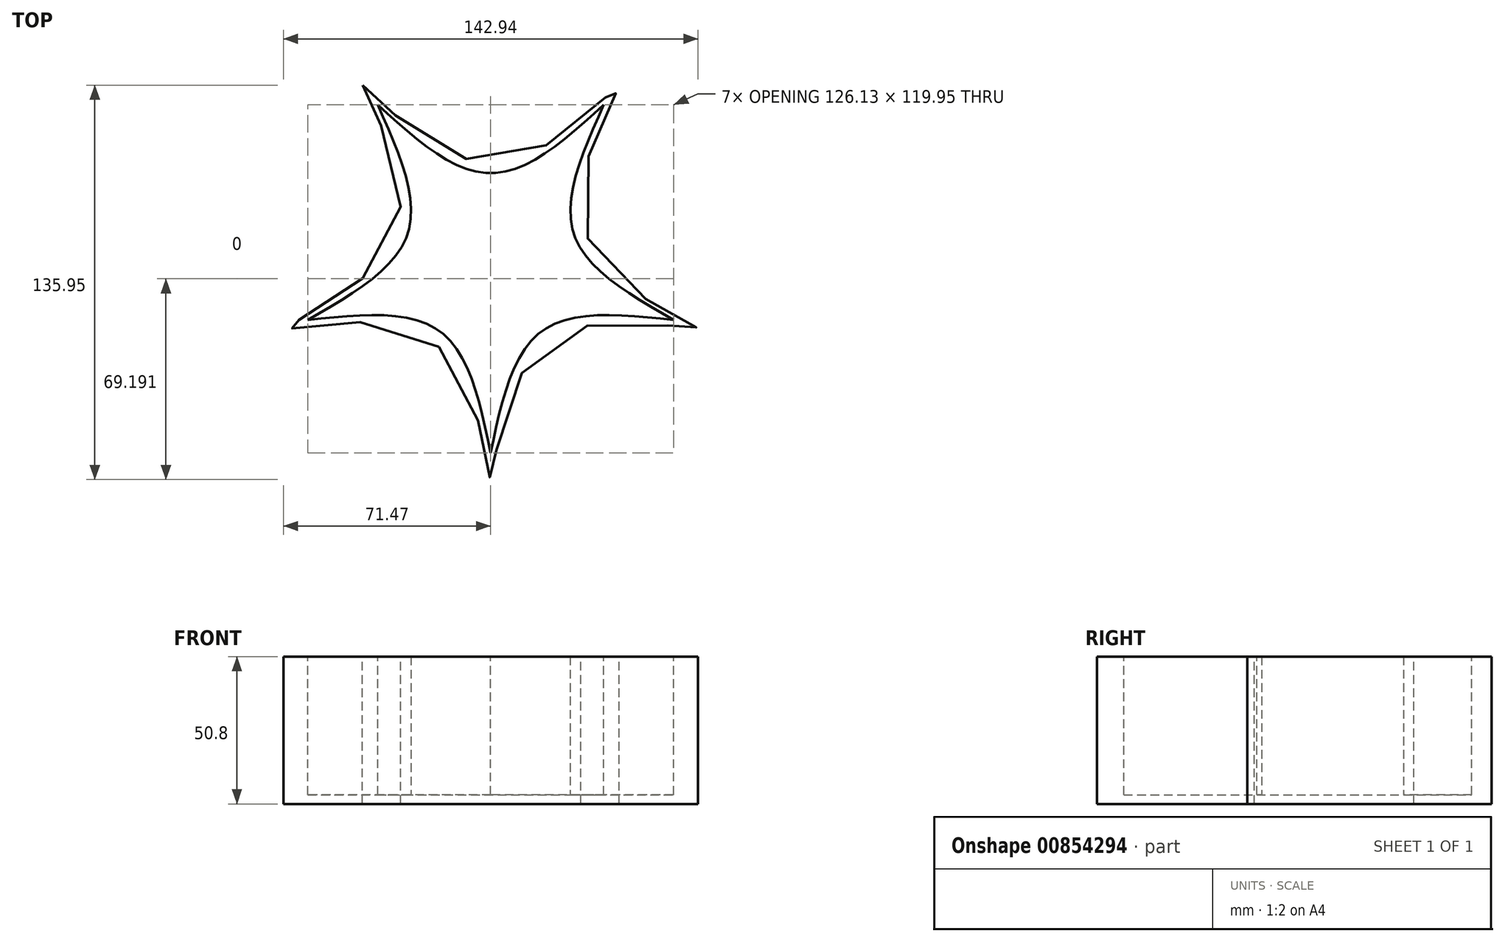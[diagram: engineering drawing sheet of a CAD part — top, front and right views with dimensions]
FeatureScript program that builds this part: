
annotation { "Feature Type Name" : "Feature", "Feature Type Description" : "" }
export const myFeature = defineFeature(function(context is Context, id is Id, definition is map)
    precondition{}
    {
        {
            var Q0;
            Q0=qCreatedBy(makeId("Top.planeOp"),FACE);
            var sketch = newSketch(context, id + "F0", { "sketchPlane" : qUnion([Q0])});
            skPoint(sketch, "E0.0.midPoint", {"position": v(0, 34.08) * mm});
            skPoint(sketch, "E1", {"position": v(71.46, -23.22) * mm});
            skPoint(sketch, "E2", {"position": v(0, -75.14) * mm});
            skPoint(sketch, "E3", {"position": v(-71.46, -23.22) * mm});
            skPoint(sketch, "E4", {"position": v(-44.17, 60.8) * mm});
            skPoint(sketch, "E5", {"position": v(44.17, 60.8) * mm});
            skFitSpline(sketch, "E6", {"points": [v(-44.17, 60.8) * mm, v(0, 34.08) * mm, v(44.17, 60.8) * mm, v(32.4, 10.53) * mm, v(71.46, -23.22) * mm, v(20.03, -27.57) * mm, v(0, -75.14) * mm, v(-20.03, -27.57) * mm, v(-71.46, -23.22) * mm, v(-32.4, 10.53) * mm, v(-44.17, 60.8) * mm]});
            skSolve(sketch);
        }
        {
            var Q0;
            Q0=qCreatedBy(makeId("Top.planeOp"),FACE);
            var sketch = newSketch(context, id + "F1", { "sketchPlane" : qUnion([Q0])});
            skPoint(sketch, "E7", {"position": v(-38.98, 54.03) * mm});
            skPoint(sketch, "E8", {"position": v(0, 30.45) * mm});
            skPoint(sketch, "E9", {"position": v(38.98, 54.03) * mm});
            skPoint(sketch, "E10", {"position": v(28.6, 9.68) * mm});
            skPoint(sketch, "E11", {"position": v(63.06, -20.1) * mm});
            skPoint(sketch, "E12", {"position": v(17.68, -23.95) * mm});
            skPoint(sketch, "E13", {"position": v(0, -65.93) * mm});
            skPoint(sketch, "E14", {"position": v(-17.68, -23.95) * mm});
            skPoint(sketch, "E15", {"position": v(-63.06, -20.1) * mm});
            skPoint(sketch, "E16", {"position": v(-28.6, 9.68) * mm});
            skFitSpline(sketch, "E17", {"points": [v(-38.98, 54.03) * mm, v(0, 30.45) * mm, v(38.98, 54.03) * mm], "startDerivative": vector(77.95, -70.72) * mm, "endDerivative": vector(77.95, 70.72) * mm});
            skFitSpline(sketch, "E18", {"points": [v(38.98, 54.03) * mm, v(28.6, 9.68) * mm, v(63.06, -20.1) * mm], "startDerivative": vector(-43.17, -95.99) * mm, "endDerivative": vector(91.34, -52.28) * mm});
            skFitSpline(sketch, "E19", {"points": [v(63.06, -20.1) * mm, v(17.68, -23.95) * mm, v(0, -65.93) * mm], "startDerivative": vector(-104.63, 11.4) * mm, "endDerivative": vector(-21.5, -103.03) * mm});
            skFitSpline(sketch, "E20", {"points": [v(0, -65.93) * mm, v(-17.68, -23.95) * mm, v(-63.06, -20.1) * mm], "startDerivative": vector(-21.5, 103.03) * mm, "endDerivative": vector(-104.63, -11.4) * mm});
            skFitSpline(sketch, "E21", {"points": [v(-63.06, -20.1) * mm, v(-28.6, 9.68) * mm, v(-38.98, 54.03) * mm], "startDerivative": vector(91.34, 52.28) * mm, "endDerivative": vector(-43.17, 95.99) * mm});
            skSolve(sketch);
        }
        {
            var Q0;
            Q0 = qSketchRegion(id + "F0", true);
            extrude(context, id + "F2", {"entities" : qUnion([Q0]), "depth" : -50.8 * mm, "offsetDistance" : 25.4 * mm});
        }
        {
            var Q0;
            Q0 = qSketchRegion(id + "F1", true);
            extrude(context, id + "F3", {"entities" : qUnion([Q0]), "operationType" : NewBodyOperationType.REMOVE, "oppositeDirection" : true, "depth" : 47.62 * mm, "offsetDistance" : 25.4 * mm});
        }
    });
